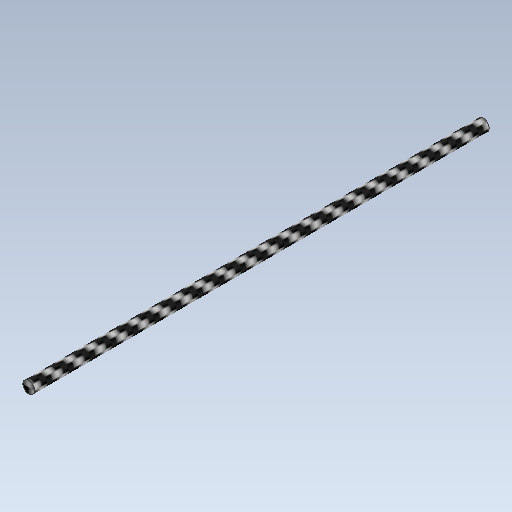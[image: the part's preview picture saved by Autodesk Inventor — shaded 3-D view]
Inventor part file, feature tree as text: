
AUTODESK INVENTOR PART (.ipt)
format: ipt  version: 2020 (Build 240168000, 168)  size: 103,936 bytes
history: native  units: in
note: dims shown in document units (in); Inventor stores cm internally (conversion verified against a paired STEP export)
features: extrude x1, sketch x1
ambient origin geometry x8: Origin, YZ Plane, XZ Plane, XY Plane, X Axis, Y Axis, Z Axis, Center Point
bodies: Solid1 (feature_tree)
feature tree (2):
  extrude  "Extrusion1"  Depth=3.1106in
  sketch  "Sketch1"  dims[d0=0.0827in d1=3.1106in d2=0.0in]
